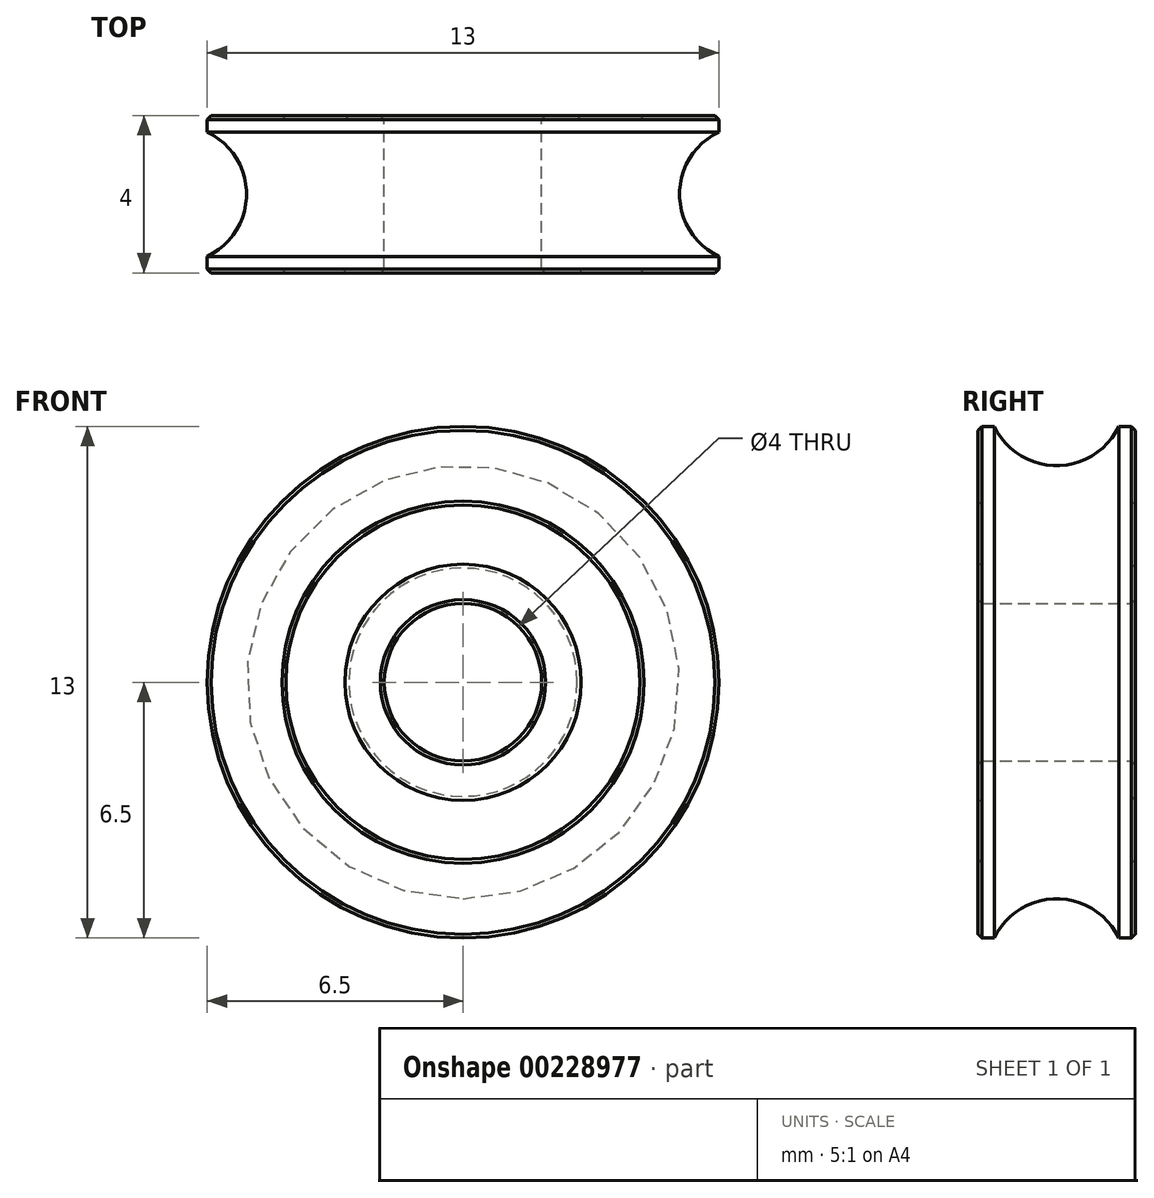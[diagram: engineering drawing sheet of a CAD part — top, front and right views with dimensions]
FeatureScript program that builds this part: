
annotation { "Feature Type Name" : "Feature", "Feature Type Description" : "" }
export const myFeature = defineFeature(function(context is Context, id is Id, definition is map)
    precondition{}
    {
        {
            var Q0;
            Q0=qCreatedBy(makeId("Front.planeOp"),FACE);
            var sketch = newSketch(context, id + "F0", { "sketchPlane" : qUnion([Q0])});
            skCircle(sketch, "E0", {"center": v(0, 0) * mm, "radius": 6.5 * mm});
            skCircle(sketch, "E1", {"center": v(0, 0) * mm, "radius": 2 * mm});
            skCircle(sketch, "E2.0", {"center": v(0, 0) * mm, "radius": 3 * mm});
            skCircle(sketch, "E3.0", {"center": v(0, 0) * mm, "radius": 4.5 * mm});
            skSolve(sketch);
        }
        {
            var Q0;
            Q0=makeQuery(id+"F0.imprint","IMPRINT",FACE,{"disambiguationData":[TD([[makeQuery(id+"F0.imprint","IMPRINT",EDGE,{"derivedFrom":sQuery(id+"F0.wireOp",EDGE,"E2.0")}),-1.0]])]});
            extrude(context, id + "F1", {"entities" : qUnion([Q0]), "endBound" : BoundingType.SYMMETRIC, "depth" : 3.8 * mm});
        }
        {
            var Q0;
            Q0=makeQuery(id+"F0.imprint","IMPRINT",FACE,{"disambiguationData":[TD([[makeQuery(id+"F0.imprint","IMPRINT",EDGE,{"derivedFrom":sQuery(id+"F0.wireOp",EDGE,"E1")}),-1.0]])]});
            var Q1;
            Q1=makeQuery(id+"F0.imprint","IMPRINT",FACE,{"disambiguationData":[TD([[makeQuery(id+"F0.imprint","IMPRINT",EDGE,{"derivedFrom":sQuery(id+"F0.wireOp",EDGE,"E0")}),1.0]])]});
            extrude(context, id + "F2", {"entities" : qUnion([Q0, Q1]), "operationType" : NewBodyOperationType.ADD, "endBound" : BoundingType.SYMMETRIC, "depth" : 4 * mm});
        }
        {
            var Q0;
            Q0=qCreatedBy(makeId("Right.planeOp"),FACE);
            var sketch = newSketch(context, id + "F3", { "sketchPlane" : qUnion([Q0])});
            skCircle(sketch, "E4", {"center": v(0, 7.25) * mm, "radius": 1.75 * mm});
            skSolve(sketch);
        }
        {
            var Q0;
            Q0=makeQuery(id+"F3.imprint","IMPRINT",FACE,{"disambiguationData":[TD([[makeQuery(id+"F3.imprint","IMPRINT",EDGE,{"derivedFrom":sQuery(id+"F3.wireOp",EDGE,"E4")}),1.0]])]});
            var Q1;
            Q1=makeQuery(id+"F2.opExtrude","CAP_EDGE",EDGE,{"disambiguationData":[OSD([sQuery(id+"F0.wireOp",EDGE,"E0")])],"isStart":false});
            sweep(context, id + "F4", {"operationType" : NewBodyOperationType.REMOVE, "profiles" : qUnion([Q0]), "path" : qUnion([Q1])});
        }
        {
            var Q0;
            Q0=makeQuery(id+"F2.opExtrude","CAP_EDGE",EDGE,{"disambiguationData":[OSD([sQuery(id+"F0.wireOp",EDGE,"E0")])],"isStart":false});
            var Q1;
            Q1=makeQuery(id+"F2.opExtrude","CAP_EDGE",EDGE,{"disambiguationData":[OSD([sQuery(id+"F0.wireOp",EDGE,"E3.0")])],"isStart":false});
            var Q2;
            Q2=makeQuery(id+"F1.opExtrude","CAP_EDGE",EDGE,{"disambiguationData":[OSD([sQuery(id+"F0.wireOp",EDGE,"E2.0")])],"isStart":false});
            var Q3;
            Q3=makeQuery(id+"F2.opExtrude","CAP_EDGE",EDGE,{"disambiguationData":[OSD([sQuery(id+"F0.wireOp",EDGE,"E1")])],"isStart":false});
            var Q4;
            Q4=makeQuery(id+"F2.opExtrude","CAP_EDGE",EDGE,{"disambiguationData":[OSD([sQuery(id+"F0.wireOp",EDGE,"E1")])],"isStart":true});
            var Q5;
            Q5=makeQuery(id+"F2.opExtrude","CAP_EDGE",EDGE,{"disambiguationData":[OSD([sQuery(id+"F0.wireOp",EDGE,"E2.0")])],"isStart":true});
            var Q6;
            Q6=makeQuery(id+"F2.opExtrude","CAP_EDGE",EDGE,{"disambiguationData":[OSD([sQuery(id+"F0.wireOp",EDGE,"E3.0")])],"isStart":true});
            var Q7;
            Q7=makeQuery(id+"F2.opExtrude","CAP_EDGE",EDGE,{"disambiguationData":[OSD([sQuery(id+"F0.wireOp",EDGE,"E0")])],"isStart":true});
            chamfer(context, id + "F5", {"entities" : qUnion([Q0, Q1, Q2, Q3, Q4, Q5, Q6, Q7]), "width" : 0.1 * mm, "tangentPropagation" : true});
        }
    });
